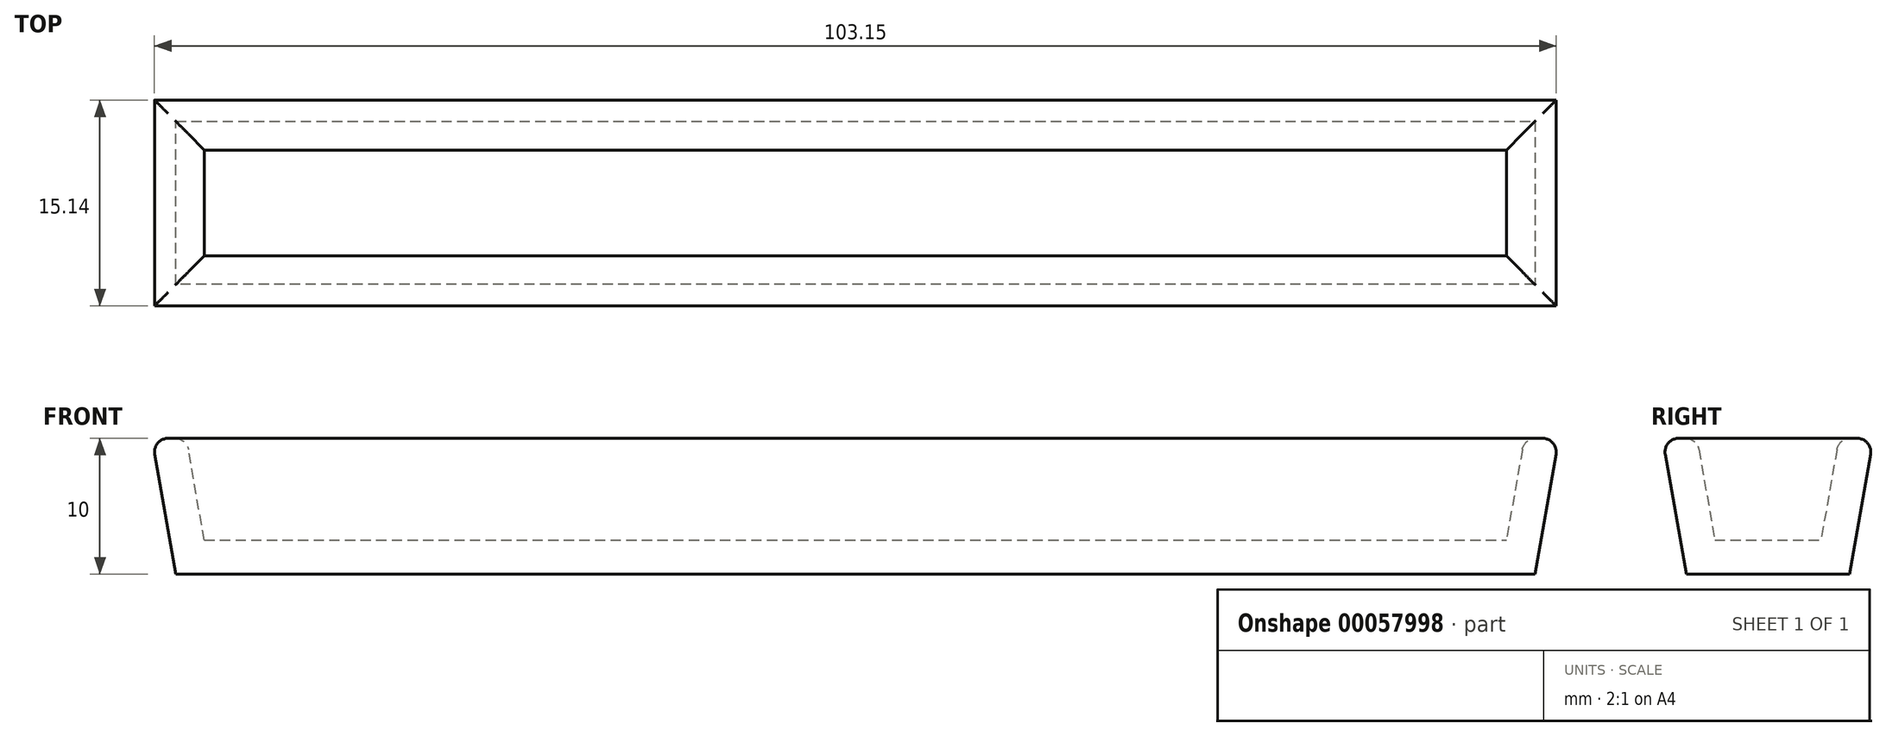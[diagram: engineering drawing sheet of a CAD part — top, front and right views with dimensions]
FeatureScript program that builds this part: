
annotation { "Feature Type Name" : "Feature", "Feature Type Description" : "" }
export const myFeature = defineFeature(function(context is Context, id is Id, definition is map)
    precondition{}
    {
        {
            var Q0;
            Q0=qCreatedBy(makeId("Top.planeOp"),FACE);
            var sketch = newSketch(context, id + "F0", { "sketchPlane" : qUnion([Q0])});
            skLineSegment(sketch, "E0.bottom", {"start": v(-51.48, -28.96) * mm, "end": v(48.52, -28.96) * mm});
            skLineSegment(sketch, "E0.top", {"start": v(-51.48, -40.96) * mm, "end": v(48.52, -40.96) * mm});
            skLineSegment(sketch, "E0.left", {"start": v(-51.48, -28.96) * mm, "end": v(-51.48, -40.96) * mm});
            skLineSegment(sketch, "E0.right", {"start": v(48.52, -28.96) * mm, "end": v(48.52, -40.96) * mm});
            skSolve(sketch);
        }
        {
            var Q0;
            Q0=makeQuery(id+"F0.imprint","IMPRINT",FACE,{"disambiguationData":[TD([[makeQuery(id+"F0.imprint","IMPRINT",EDGE,{"derivedFrom":sQuery(id+"F0.wireOp",EDGE,"E0.bottom")}),-1.0]])]});
            extrude(context, id + "F1", {"entities" : qUnion([Q0]), "depth" : 10 * mm, "hasDraft" : true, "draftAngle" : 10 * degree});
        }
        {
            var Q0;
            Q0=makeQuery(id+"F1.opExtrude","CAP_FACE",FACE,{"disambiguationData":[OSD([sQuery(id+"F0.wireOp",EDGE,"E0.bottom"),sQuery(id+"F0.wireOp",EDGE,"E0.top"),sQuery(id+"F0.wireOp",EDGE,"E0.left"),sQuery(id+"F0.wireOp",EDGE,"E0.right")])],"isStart":false});
            shell(context, id + "F2", {"entities" : qUnion([Q0]), "thickness" : 2.5 * mm});
        }
        {
            var Q0;
            Q0=makeQuery(id+"F1.opExtrude","CAP_EDGE",EDGE,{"disambiguationData":[OSD([sQuery(id+"F0.wireOp",EDGE,"E0.top")])],"isStart":false});
            var Q1;
            Q1=makeQuery(id+"F1.opExtrude","CAP_EDGE",EDGE,{"disambiguationData":[OSD([sQuery(id+"F0.wireOp",EDGE,"E0.left")])],"isStart":false});
            var Q2;
            Q2=makeQuery(id+"F1.opExtrude","CAP_EDGE",EDGE,{"disambiguationData":[OSD([sQuery(id+"F0.wireOp",EDGE,"E0.bottom")])],"isStart":false});
            var Q3;
            Q3=makeQuery(id+"F1.opExtrude","CAP_EDGE",EDGE,{"disambiguationData":[OSD([sQuery(id+"F0.wireOp",EDGE,"E0.right")])],"isStart":false});
            var Q4;
            {var subQ0=sQuery(id+"F0.wireOp",EDGE,"E0.left");Q4=makeQuery(id+"F2.opShell","OFFSET_EDGE",EDGE,{"disambiguationData":[OSD([subQ0]),TDD([makeQuery(id+"F1.opExtrude","CAP_EDGE",EDGE,{"disambiguationData":[OSD([subQ0])],"isStart":false})])]});}
            var Q5;
            {var subQ0=sQuery(id+"F0.wireOp",EDGE,"E0.bottom");Q5=makeQuery(id+"F2.opShell","OFFSET_EDGE",EDGE,{"disambiguationData":[OSD([subQ0]),TDD([makeQuery(id+"F1.opExtrude","CAP_EDGE",EDGE,{"disambiguationData":[OSD([subQ0])],"isStart":false})])]});}
            var Q6;
            {var subQ0=sQuery(id+"F0.wireOp",EDGE,"E0.top");Q6=makeQuery(id+"F2.opShell","OFFSET_EDGE",EDGE,{"disambiguationData":[OSD([subQ0]),TDD([makeQuery(id+"F1.opExtrude","CAP_EDGE",EDGE,{"disambiguationData":[OSD([subQ0])],"isStart":false})])]});}
            var Q7;
            {var subQ0=sQuery(id+"F0.wireOp",EDGE,"E0.right");Q7=makeQuery(id+"F2.opShell","OFFSET_EDGE",EDGE,{"disambiguationData":[OSD([subQ0]),TDD([makeQuery(id+"F1.opExtrude","CAP_EDGE",EDGE,{"disambiguationData":[OSD([subQ0])],"isStart":false})])]});}
            fillet(context, id + "F3", {"entities" : qUnion([Q0, Q1, Q2, Q3, Q4, Q5, Q6, Q7]), "radius" : 1 * mm, "tangentPropagation" : true, "allowEdgeOverflow" : false});
        }
    });
